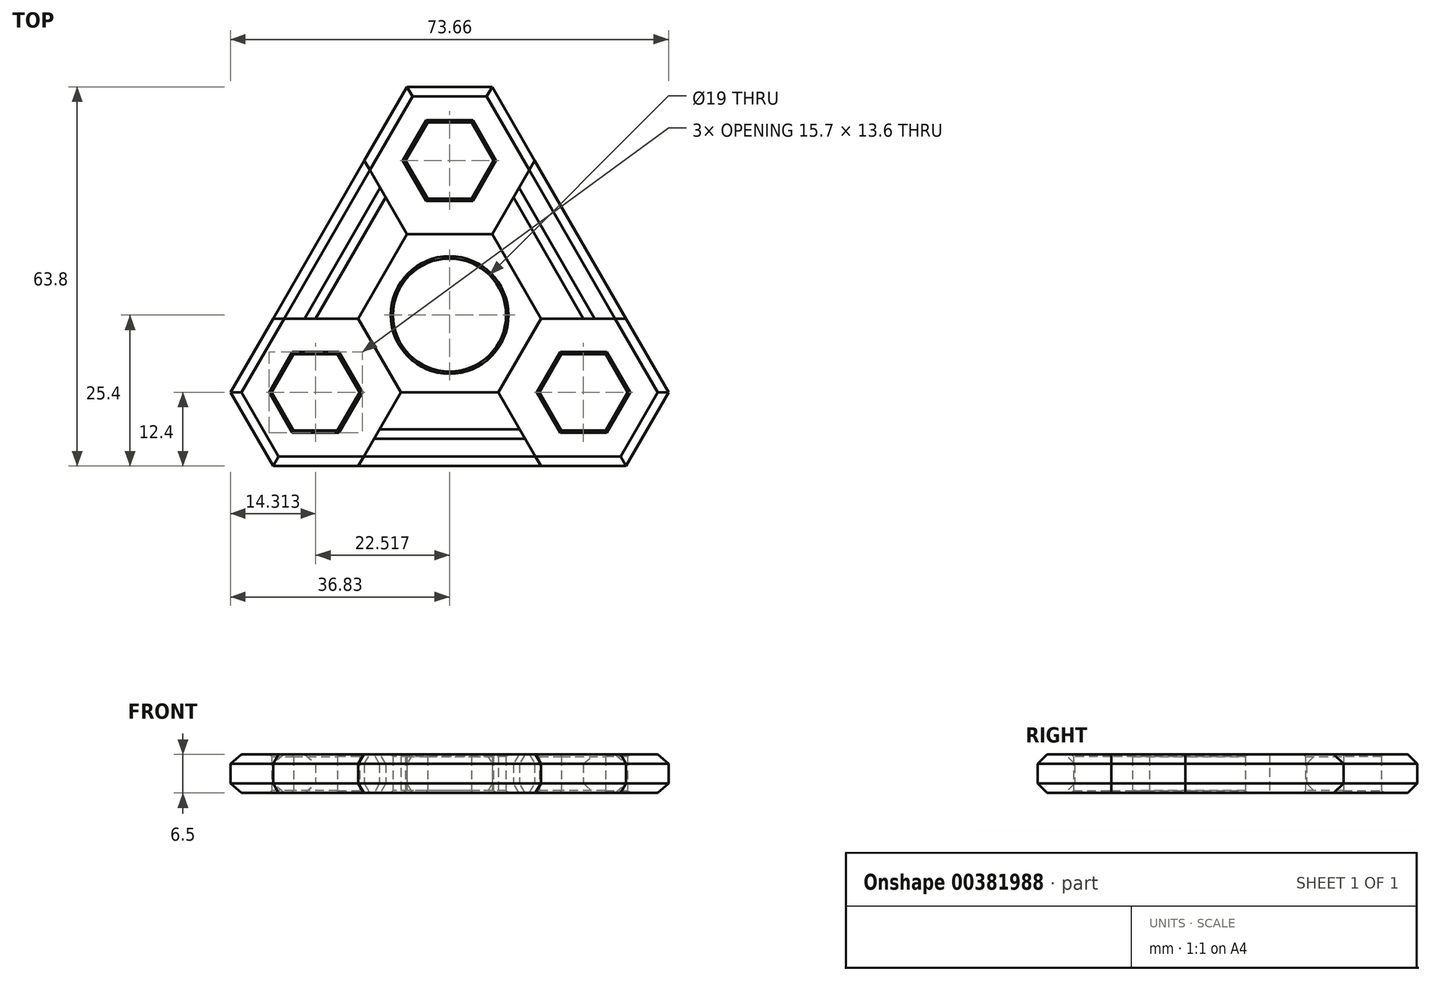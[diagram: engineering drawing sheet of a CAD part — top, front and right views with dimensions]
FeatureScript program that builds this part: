
annotation { "Feature Type Name" : "Feature", "Feature Type Description" : "" }
export const myFeature = defineFeature(function(context is Context, id is Id, definition is map)
    precondition{}
    {
        {
            var Q0;
            Q0=qCreatedBy(makeId("Top.planeOp"),FACE);
            var sketch = newSketch(context, id + "F0", { "sketchPlane" : qUnion([Q0])});
            skCircle(sketch, "E0", {"center": v(0, 0) * mm, "radius": 9.5 * mm});
            skCircle(sketch, "E1.cCircle", {"center": v(0, 26) * mm, "radius": 6.4 * mm, "construction": true});
            skLineSegment(sketch, "E1.0", {"start": v(3.7, 19.6) * mm, "end": v(-3.7, 19.6) * mm});
            skLineSegment(sketch, "E1.1", {"start": v(-3.7, 19.6) * mm, "end": v(-7.4, 26) * mm});
            skLineSegment(sketch, "E1.2", {"start": v(-7.4, 26) * mm, "end": v(-3.7, 32.4) * mm});
            skLineSegment(sketch, "E1.3", {"start": v(-3.7, 32.4) * mm, "end": v(3.7, 32.4) * mm});
            skLineSegment(sketch, "E1.4", {"start": v(3.7, 32.4) * mm, "end": v(7.4, 26) * mm});
            skLineSegment(sketch, "E1.5", {"start": v(7.4, 26) * mm, "end": v(3.7, 19.6) * mm});
            skPoint(sketch, "E1.0.midPoint", {"position": v(0, 19.6) * mm});
            skLineSegment(sketch, "E2.1.0", {"start": v(-26.21, -19.4) * mm, "end": v(-29.9, -13) * mm});
            skLineSegment(sketch, "E2.1.1", {"start": v(-29.9, -13) * mm, "end": v(-26.21, -6.6) * mm});
            skLineSegment(sketch, "E2.1.2", {"start": v(-26.21, -6.6) * mm, "end": v(-18.82, -6.6) * mm});
            skLineSegment(sketch, "E2.1.3", {"start": v(-18.82, -6.6) * mm, "end": v(-15.13, -13) * mm});
            skLineSegment(sketch, "E2.1.4", {"start": v(-15.13, -13) * mm, "end": v(-18.82, -19.4) * mm});
            skLineSegment(sketch, "E2.1.5", {"start": v(-18.82, -19.4) * mm, "end": v(-26.21, -19.4) * mm});
            skCircle(sketch, "E2.1.6", {"center": v(-22.52, -13) * mm, "radius": 6.4 * mm, "construction": true});
            skLineSegment(sketch, "E2.2.0", {"start": v(29.9, -13) * mm, "end": v(26.21, -19.4) * mm});
            skLineSegment(sketch, "E2.2.1", {"start": v(26.21, -19.4) * mm, "end": v(18.82, -19.4) * mm});
            skLineSegment(sketch, "E2.2.2", {"start": v(18.82, -19.4) * mm, "end": v(15.13, -13) * mm});
            skLineSegment(sketch, "E2.2.3", {"start": v(15.13, -13) * mm, "end": v(18.82, -6.6) * mm});
            skLineSegment(sketch, "E2.2.4", {"start": v(18.82, -6.6) * mm, "end": v(26.21, -6.6) * mm});
            skLineSegment(sketch, "E2.2.5", {"start": v(26.21, -6.6) * mm, "end": v(29.9, -13) * mm});
            skCircle(sketch, "E2.2.6", {"center": v(22.52, -13) * mm, "radius": 6.4 * mm, "construction": true});
            skLineSegment(sketch, "E3.0", {"start": v(-7.16, 13.6) * mm, "end": v(-14.32, 26) * mm});
            skLineSegment(sketch, "E3.1", {"start": v(-7.16, 38.4) * mm, "end": v(7.16, 38.4) * mm});
            skLineSegment(sketch, "E3.2", {"start": v(7.16, 38.4) * mm, "end": v(14.32, 26) * mm});
            skLineSegment(sketch, "E3.3", {"start": v(-14.32, 26) * mm, "end": v(-7.16, 38.4) * mm});
            skLineSegment(sketch, "E3.4", {"start": v(14.32, 26) * mm, "end": v(7.16, 13.6) * mm});
            skLineSegment(sketch, "E3.5", {"start": v(7.16, 13.6) * mm, "end": v(-7.16, 13.6) * mm});
            skLineSegment(sketch, "E4.1.0", {"start": v(-15.36, -25.4) * mm, "end": v(-29.68, -25.4) * mm});
            skLineSegment(sketch, "E4.1.1", {"start": v(-29.68, -25.4) * mm, "end": v(-36.83, -13) * mm});
            skLineSegment(sketch, "E4.1.2", {"start": v(-36.83, -13) * mm, "end": v(-29.68, -0.6) * mm});
            skLineSegment(sketch, "E4.1.3", {"start": v(-29.68, -0.6) * mm, "end": v(-15.36, -0.6) * mm});
            skLineSegment(sketch, "E4.1.4", {"start": v(-15.36, -0.6) * mm, "end": v(-8.2, -13) * mm});
            skLineSegment(sketch, "E4.1.5", {"start": v(-8.2, -13) * mm, "end": v(-15.36, -25.4) * mm});
            skLineSegment(sketch, "E4.2.0", {"start": v(29.68, -0.6) * mm, "end": v(36.83, -13) * mm});
            skLineSegment(sketch, "E4.2.1", {"start": v(36.83, -13) * mm, "end": v(29.68, -25.4) * mm});
            skLineSegment(sketch, "E4.2.2", {"start": v(29.68, -25.4) * mm, "end": v(15.36, -25.4) * mm});
            skLineSegment(sketch, "E4.2.3", {"start": v(15.36, -25.4) * mm, "end": v(8.2, -13) * mm});
            skLineSegment(sketch, "E4.2.4", {"start": v(8.2, -13) * mm, "end": v(15.36, -0.6) * mm});
            skLineSegment(sketch, "E4.2.5", {"start": v(15.36, -0.6) * mm, "end": v(29.68, -0.6) * mm});
            skLineSegment(sketch, "E5", {"start": v(-14.32, 26) * mm, "end": v(-29.68, -0.6) * mm});
            skLineSegment(sketch, "E6", {"start": v(-7.16, 13.6) * mm, "end": v(-15.36, -0.6) * mm});
            skLineSegment(sketch, "E7", {"start": v(-8.2, -13) * mm, "end": v(8.2, -13) * mm});
            skLineSegment(sketch, "E8", {"start": v(15.36, -0.6) * mm, "end": v(7.16, 13.6) * mm});
            skLineSegment(sketch, "E9", {"start": v(14.32, 26) * mm, "end": v(29.68, -0.6) * mm});
            skLineSegment(sketch, "E10", {"start": v(15.36, -25.4) * mm, "end": v(-15.36, -25.4) * mm});
            skLineSegment(sketch, "E11", {"start": v(-11.78, -19.2) * mm, "end": v(11.78, -19.2) * mm});
            skLineSegment(sketch, "E12", {"start": v(22.52, -0.6) * mm, "end": v(10.74, 19.8) * mm});
            skLineSegment(sketch, "E13", {"start": v(-10.74, 19.8) * mm, "end": v(-22.52, -0.6) * mm});
            skSolve(sketch);
        }
        {
            var Q0;
            Q0=makeQuery(id+"F0.imprint","IMPRINT",FACE,{"disambiguationData":[TD([[makeQuery(id+"F0.imprint","IMPRINT",EDGE,{"derivedFrom":sQuery(id+"F0.wireOp",EDGE,"E1.0")}),1.0]])]});
            var Q1;
            Q1=makeQuery(id+"F0.imprint","IMPRINT",FACE,{"disambiguationData":[TD([[makeQuery(id+"F0.imprint","IMPRINT",EDGE,{"derivedFrom":sQuery(id+"F0.wireOp",EDGE,"E2.1.0")}),1.0]])]});
            var Q2;
            Q2=makeQuery(id+"F0.imprint","IMPRINT",FACE,{"disambiguationData":[TD([[makeQuery(id+"F0.imprint","IMPRINT",EDGE,{"derivedFrom":sQuery(id+"F0.wireOp",EDGE,"E2.2.0")}),1.0]])]});
            extrude(context, id + "F1", {"entities" : qUnion([Q0, Q1, Q2]), "depth" : 6.5 * mm, "offsetDistance" : 25 * mm});
        }
        {
            var Q0;
            {var subQ0=sQuery(id+"F0.wireOp",EDGE,"E5");Q0=makeQuery(id+"F0.imprint","IMPRINT",FACE,{"disambiguationData":[TD([[makeQuery(id+"F0.imprint","IMPRINT",EDGE,{"derivedFrom":subQ0}),1.0]])]});}
            var Q1;
            Q1=makeQuery(id+"F0.imprint","IMPRINT",FACE,{"disambiguationData":[TD([[makeQuery(id+"F0.imprint","IMPRINT",EDGE,{"derivedFrom":sQuery(id+"F0.wireOp",EDGE,"E0")}),-1.0]])]});
            var Q2;
            {var subQ0=sQuery(id+"F0.wireOp",EDGE,"E10");Q2=makeQuery(id+"F0.imprint","IMPRINT",FACE,{"disambiguationData":[TD([[makeQuery(id+"F0.imprint","IMPRINT",EDGE,{"derivedFrom":subQ0}),-1.0]])]});}
            var Q3;
            {var subQ0=sQuery(id+"F0.wireOp",EDGE,"E9");Q3=makeQuery(id+"F0.imprint","IMPRINT",FACE,{"disambiguationData":[TD([[makeQuery(id+"F0.imprint","IMPRINT",EDGE,{"derivedFrom":subQ0}),-1.0]])]});}
            extrude(context, id + "F2", {"entities" : qUnion([Q0, Q1, Q2, Q3]), "depth" : 6.5 * mm, "offsetDistance" : 25 * mm});
        }
        {
            var Q0;
            Q0=makeQuery(id+"F2.opExtrude","CAP_EDGE",EDGE,{"disambiguationData":[OSD([sQuery(id+"F0.wireOp",EDGE,"E5")])],"isStart":false});
            var Q1;
            Q1=makeQuery(id+"F2.opExtrude","CAP_EDGE",EDGE,{"disambiguationData":[OSD([sQuery(id+"F0.wireOp",EDGE,"E5")])],"isStart":true});
            var Q2;
            Q2=makeQuery(id+"F2.opExtrude","CAP_EDGE",EDGE,{"disambiguationData":[OSD([sQuery(id+"F0.wireOp",EDGE,"E10")])],"isStart":false});
            var Q3;
            Q3=makeQuery(id+"F2.opExtrude","CAP_EDGE",EDGE,{"disambiguationData":[OSD([sQuery(id+"F0.wireOp",EDGE,"E10")])],"isStart":true});
            var Q4;
            Q4=makeQuery(id+"F2.opExtrude","CAP_EDGE",EDGE,{"disambiguationData":[OSD([sQuery(id+"F0.wireOp",EDGE,"E9")])],"isStart":false});
            var Q5;
            Q5=makeQuery(id+"F2.opExtrude","CAP_EDGE",EDGE,{"disambiguationData":[OSD([sQuery(id+"F0.wireOp",EDGE,"E9")])],"isStart":true});
            var Q6;
            Q6=makeQuery(id+"F2.opExtrude","CAP_EDGE",EDGE,{"disambiguationData":[OSD([sQuery(id+"F0.wireOp",EDGE,"E12")])],"isStart":false});
            var Q7;
            Q7=makeQuery(id+"F2.opExtrude","CAP_EDGE",EDGE,{"disambiguationData":[OSD([sQuery(id+"F0.wireOp",EDGE,"E11")])],"isStart":false});
            var Q8;
            Q8=makeQuery(id+"F2.opExtrude","CAP_EDGE",EDGE,{"disambiguationData":[OSD([sQuery(id+"F0.wireOp",EDGE,"E13")])],"isStart":true});
            var Q9;
            Q9=makeQuery(id+"F2.opExtrude","CAP_EDGE",EDGE,{"disambiguationData":[OSD([sQuery(id+"F0.wireOp",EDGE,"E13")])],"isStart":false});
            var Q10;
            Q10=makeQuery(id+"F2.opExtrude","CAP_EDGE",EDGE,{"disambiguationData":[OSD([sQuery(id+"F0.wireOp",EDGE,"E12")])],"isStart":true});
            var Q11;
            Q11=makeQuery(id+"F2.opExtrude","CAP_EDGE",EDGE,{"disambiguationData":[OSD([sQuery(id+"F0.wireOp",EDGE,"E11")])],"isStart":true});
            chamfer(context, id + "F3", {"entities" : qUnion([Q0, Q1, Q2, Q3, Q4, Q5, Q6, Q7, Q8, Q9, Q10, Q11]), "width" : 1.6 * mm, "tangentPropagation" : true});
        }
        {
            var Q0;
            Q0=makeQuery(id+"F1.opExtrude","CAP_EDGE",EDGE,{"disambiguationData":[OSD([sQuery(id+"F0.wireOp",EDGE,"E3.3")])],"isStart":false});
            var Q1;
            Q1=makeQuery(id+"F1.opExtrude","CAP_EDGE",EDGE,{"disambiguationData":[OSD([sQuery(id+"F0.wireOp",EDGE,"E3.3")])],"isStart":true});
            var Q2;
            Q2=makeQuery(id+"F1.opExtrude","CAP_EDGE",EDGE,{"disambiguationData":[OSD([sQuery(id+"F0.wireOp",EDGE,"E4.1.2")])],"isStart":false});
            var Q3;
            Q3=makeQuery(id+"F1.opExtrude","CAP_EDGE",EDGE,{"disambiguationData":[OSD([sQuery(id+"F0.wireOp",EDGE,"E4.1.2")])],"isStart":true});
            var Q4;
            Q4=makeQuery(id+"F1.opExtrude","CAP_EDGE",EDGE,{"disambiguationData":[OSD([sQuery(id+"F0.wireOp",EDGE,"E3.2")])],"isStart":false});
            var Q5;
            Q5=makeQuery(id+"F1.opExtrude","CAP_EDGE",EDGE,{"disambiguationData":[OSD([sQuery(id+"F0.wireOp",EDGE,"E3.2")])],"isStart":true});
            var Q6;
            Q6=makeQuery(id+"F1.opExtrude","CAP_EDGE",EDGE,{"disambiguationData":[OSD([sQuery(id+"F0.wireOp",EDGE,"E4.2.0")])],"isStart":false});
            var Q7;
            Q7=makeQuery(id+"F1.opExtrude","CAP_EDGE",EDGE,{"disambiguationData":[OSD([sQuery(id+"F0.wireOp",EDGE,"E4.2.0")])],"isStart":true});
            var Q8;
            Q8=makeQuery(id+"F1.opExtrude","CAP_EDGE",EDGE,{"disambiguationData":[OSD([sQuery(id+"F0.wireOp",EDGE,"E4.2.2")])],"isStart":false});
            var Q9;
            Q9=makeQuery(id+"F1.opExtrude","CAP_EDGE",EDGE,{"disambiguationData":[OSD([sQuery(id+"F0.wireOp",EDGE,"E4.2.2")])],"isStart":true});
            var Q10;
            Q10=makeQuery(id+"F1.opExtrude","CAP_EDGE",EDGE,{"disambiguationData":[OSD([sQuery(id+"F0.wireOp",EDGE,"E4.1.0")])],"isStart":false});
            var Q11;
            Q11=makeQuery(id+"F1.opExtrude","CAP_EDGE",EDGE,{"disambiguationData":[OSD([sQuery(id+"F0.wireOp",EDGE,"E4.1.0")])],"isStart":true});
            var Q12;
            Q12=makeQuery(id+"F1.opExtrude","CAP_EDGE",EDGE,{"disambiguationData":[OSD([sQuery(id+"F0.wireOp",EDGE,"E4.2.1")])],"isStart":false});
            var Q13;
            Q13=makeQuery(id+"F1.opExtrude","CAP_EDGE",EDGE,{"disambiguationData":[OSD([sQuery(id+"F0.wireOp",EDGE,"E4.2.1")])],"isStart":true});
            var Q14;
            Q14=makeQuery(id+"F1.opExtrude","CAP_EDGE",EDGE,{"disambiguationData":[OSD([sQuery(id+"F0.wireOp",EDGE,"E4.1.1")])],"isStart":false});
            var Q15;
            Q15=makeQuery(id+"F1.opExtrude","CAP_EDGE",EDGE,{"disambiguationData":[OSD([sQuery(id+"F0.wireOp",EDGE,"E4.1.1")])],"isStart":true});
            var Q16;
            Q16=makeQuery(id+"F1.opExtrude","CAP_EDGE",EDGE,{"disambiguationData":[OSD([sQuery(id+"F0.wireOp",EDGE,"E3.1")])],"isStart":false});
            var Q17;
            Q17=makeQuery(id+"F1.opExtrude","CAP_EDGE",EDGE,{"disambiguationData":[OSD([sQuery(id+"F0.wireOp",EDGE,"E3.1")])],"isStart":true});
            chamfer(context, id + "F4", {"entities" : qUnion([Q0, Q1, Q2, Q3, Q4, Q5, Q6, Q7, Q8, Q9, Q10, Q11, Q12, Q13, Q14, Q15, Q16, Q17]), "width" : 1.6 * mm, "tangentPropagation" : true});
        }
        {
            var Q0;
            Q0=makeQuery(id+"F2.opExtrude","CAP_EDGE",EDGE,{"disambiguationData":[OSD([sQuery(id+"F0.wireOp",EDGE,"E0")])],"isStart":false});
            var Q1;
            Q1=makeQuery(id+"F2.opExtrude","CAP_EDGE",EDGE,{"disambiguationData":[OSD([sQuery(id+"F0.wireOp",EDGE,"E0")])],"isStart":true});
            var Q2;
            Q2=makeQuery(id+"F1.opExtrude","CAP_EDGE",EDGE,{"disambiguationData":[OSD([sQuery(id+"F0.wireOp",EDGE,"E1.5")])],"isStart":false});
            var Q3;
            Q3=makeQuery(id+"F1.opExtrude","CAP_EDGE",EDGE,{"disambiguationData":[OSD([sQuery(id+"F0.wireOp",EDGE,"E1.4")])],"isStart":false});
            var Q4;
            Q4=makeQuery(id+"F1.opExtrude","CAP_EDGE",EDGE,{"disambiguationData":[OSD([sQuery(id+"F0.wireOp",EDGE,"E1.0")])],"isStart":false});
            var Q5;
            Q5=makeQuery(id+"F1.opExtrude","CAP_EDGE",EDGE,{"disambiguationData":[OSD([sQuery(id+"F0.wireOp",EDGE,"E1.1")])],"isStart":false});
            var Q6;
            Q6=makeQuery(id+"F1.opExtrude","CAP_EDGE",EDGE,{"disambiguationData":[OSD([sQuery(id+"F0.wireOp",EDGE,"E1.2")])],"isStart":false});
            var Q7;
            Q7=makeQuery(id+"F1.opExtrude","CAP_EDGE",EDGE,{"disambiguationData":[OSD([sQuery(id+"F0.wireOp",EDGE,"E1.3")])],"isStart":false});
            var Q8;
            Q8=makeQuery(id+"F1.opExtrude","CAP_EDGE",EDGE,{"disambiguationData":[OSD([sQuery(id+"F0.wireOp",EDGE,"E1.1")])],"isStart":true});
            var Q9;
            Q9=makeQuery(id+"F1.opExtrude","CAP_EDGE",EDGE,{"disambiguationData":[OSD([sQuery(id+"F0.wireOp",EDGE,"E1.0")])],"isStart":true});
            var Q10;
            Q10=makeQuery(id+"F1.opExtrude","CAP_EDGE",EDGE,{"disambiguationData":[OSD([sQuery(id+"F0.wireOp",EDGE,"E1.5")])],"isStart":true});
            var Q11;
            Q11=makeQuery(id+"F1.opExtrude","CAP_EDGE",EDGE,{"disambiguationData":[OSD([sQuery(id+"F0.wireOp",EDGE,"E1.4")])],"isStart":true});
            var Q12;
            Q12=makeQuery(id+"F1.opExtrude","CAP_EDGE",EDGE,{"disambiguationData":[OSD([sQuery(id+"F0.wireOp",EDGE,"E1.3")])],"isStart":true});
            var Q13;
            Q13=makeQuery(id+"F1.opExtrude","CAP_EDGE",EDGE,{"disambiguationData":[OSD([sQuery(id+"F0.wireOp",EDGE,"E1.2")])],"isStart":true});
            var Q14;
            Q14=makeQuery(id+"F1.opExtrude","CAP_EDGE",EDGE,{"disambiguationData":[OSD([sQuery(id+"F0.wireOp",EDGE,"E2.1.2")])],"isStart":true});
            var Q15;
            Q15=makeQuery(id+"F1.opExtrude","CAP_EDGE",EDGE,{"disambiguationData":[OSD([sQuery(id+"F0.wireOp",EDGE,"E2.1.1")])],"isStart":true});
            var Q16;
            Q16=makeQuery(id+"F1.opExtrude","CAP_EDGE",EDGE,{"disambiguationData":[OSD([sQuery(id+"F0.wireOp",EDGE,"E2.1.0")])],"isStart":true});
            var Q17;
            Q17=makeQuery(id+"F1.opExtrude","CAP_EDGE",EDGE,{"disambiguationData":[OSD([sQuery(id+"F0.wireOp",EDGE,"E2.1.5")])],"isStart":true});
            var Q18;
            Q18=makeQuery(id+"F1.opExtrude","CAP_EDGE",EDGE,{"disambiguationData":[OSD([sQuery(id+"F0.wireOp",EDGE,"E2.1.4")])],"isStart":true});
            var Q19;
            Q19=makeQuery(id+"F1.opExtrude","CAP_EDGE",EDGE,{"disambiguationData":[OSD([sQuery(id+"F0.wireOp",EDGE,"E2.1.3")])],"isStart":true});
            var Q20;
            Q20=makeQuery(id+"F1.opExtrude","CAP_EDGE",EDGE,{"disambiguationData":[OSD([sQuery(id+"F0.wireOp",EDGE,"E2.1.4")])],"isStart":false});
            var Q21;
            Q21=makeQuery(id+"F1.opExtrude","CAP_EDGE",EDGE,{"disambiguationData":[OSD([sQuery(id+"F0.wireOp",EDGE,"E2.1.3")])],"isStart":false});
            var Q22;
            Q22=makeQuery(id+"F1.opExtrude","CAP_EDGE",EDGE,{"disambiguationData":[OSD([sQuery(id+"F0.wireOp",EDGE,"E2.1.2")])],"isStart":false});
            var Q23;
            Q23=makeQuery(id+"F1.opExtrude","CAP_EDGE",EDGE,{"disambiguationData":[OSD([sQuery(id+"F0.wireOp",EDGE,"E2.1.1")])],"isStart":false});
            var Q24;
            Q24=makeQuery(id+"F1.opExtrude","CAP_EDGE",EDGE,{"disambiguationData":[OSD([sQuery(id+"F0.wireOp",EDGE,"E2.1.0")])],"isStart":false});
            var Q25;
            Q25=makeQuery(id+"F1.opExtrude","CAP_EDGE",EDGE,{"disambiguationData":[OSD([sQuery(id+"F0.wireOp",EDGE,"E2.1.5")])],"isStart":false});
            var Q26;
            Q26=makeQuery(id+"F1.opExtrude","CAP_EDGE",EDGE,{"disambiguationData":[OSD([sQuery(id+"F0.wireOp",EDGE,"E2.2.1")])],"isStart":false});
            var Q27;
            Q27=makeQuery(id+"F1.opExtrude","CAP_EDGE",EDGE,{"disambiguationData":[OSD([sQuery(id+"F0.wireOp",EDGE,"E2.2.0")])],"isStart":false});
            var Q28;
            Q28=makeQuery(id+"F1.opExtrude","CAP_EDGE",EDGE,{"disambiguationData":[OSD([sQuery(id+"F0.wireOp",EDGE,"E2.2.5")])],"isStart":false});
            var Q29;
            Q29=makeQuery(id+"F1.opExtrude","CAP_EDGE",EDGE,{"disambiguationData":[OSD([sQuery(id+"F0.wireOp",EDGE,"E2.2.4")])],"isStart":false});
            var Q30;
            Q30=makeQuery(id+"F1.opExtrude","CAP_EDGE",EDGE,{"disambiguationData":[OSD([sQuery(id+"F0.wireOp",EDGE,"E2.2.3")])],"isStart":false});
            var Q31;
            Q31=makeQuery(id+"F1.opExtrude","CAP_EDGE",EDGE,{"disambiguationData":[OSD([sQuery(id+"F0.wireOp",EDGE,"E2.2.2")])],"isStart":false});
            var Q32;
            Q32=makeQuery(id+"F1.opExtrude","CAP_EDGE",EDGE,{"disambiguationData":[OSD([sQuery(id+"F0.wireOp",EDGE,"E2.2.1")])],"isStart":true});
            var Q33;
            Q33=makeQuery(id+"F1.opExtrude","CAP_EDGE",EDGE,{"disambiguationData":[OSD([sQuery(id+"F0.wireOp",EDGE,"E2.2.2")])],"isStart":true});
            var Q34;
            Q34=makeQuery(id+"F1.opExtrude","CAP_EDGE",EDGE,{"disambiguationData":[OSD([sQuery(id+"F0.wireOp",EDGE,"E2.2.3")])],"isStart":true});
            var Q35;
            Q35=makeQuery(id+"F1.opExtrude","CAP_EDGE",EDGE,{"disambiguationData":[OSD([sQuery(id+"F0.wireOp",EDGE,"E2.2.4")])],"isStart":true});
            var Q36;
            Q36=makeQuery(id+"F1.opExtrude","CAP_EDGE",EDGE,{"disambiguationData":[OSD([sQuery(id+"F0.wireOp",EDGE,"E2.2.5")])],"isStart":true});
            var Q37;
            Q37=makeQuery(id+"F1.opExtrude","CAP_EDGE",EDGE,{"disambiguationData":[OSD([sQuery(id+"F0.wireOp",EDGE,"E2.2.0")])],"isStart":true});
            chamfer(context, id + "F5", {"entities" : qUnion([Q0, Q1, Q2, Q3, Q4, Q5, Q6, Q7, Q8, Q9, Q10, Q11, Q12, Q13, Q14, Q15, Q16, Q17, Q18, Q19, Q20, Q21, Q22, Q23, Q24, Q25, Q26, Q27, Q28, Q29, Q30, Q31, Q32, Q33, Q34, Q35, Q36, Q37]), "width" : .4 * mm, "tangentPropagation" : true});
        }
    });
